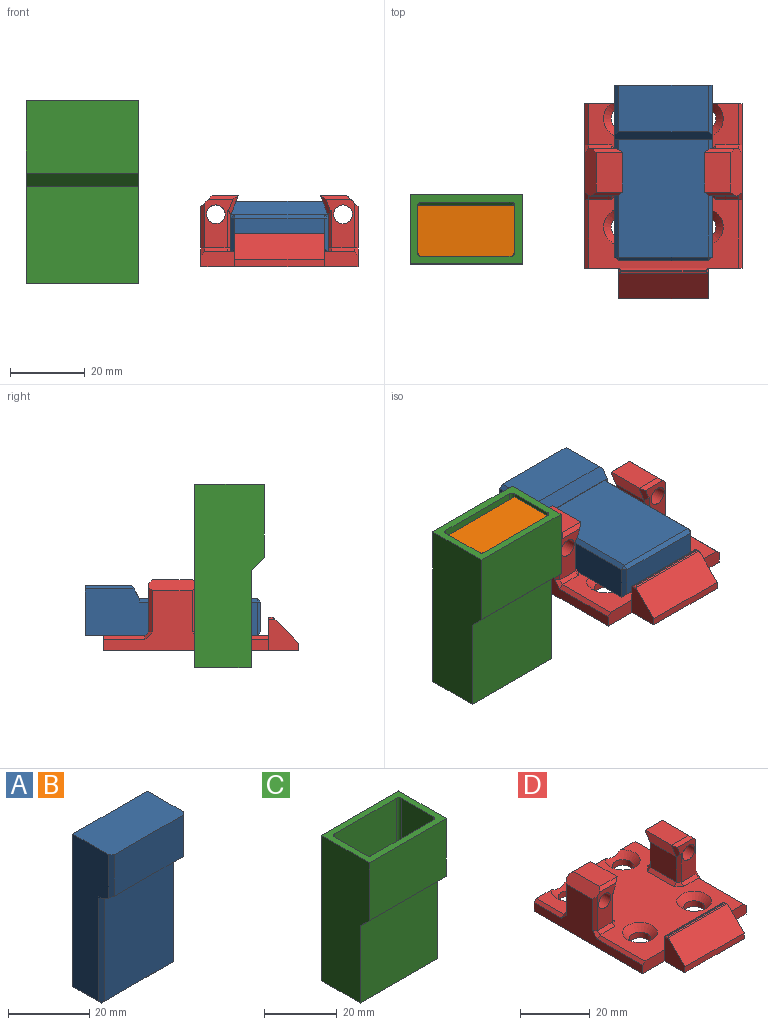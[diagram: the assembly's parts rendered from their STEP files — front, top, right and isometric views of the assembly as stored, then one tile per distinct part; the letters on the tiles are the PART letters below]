
ASSEMBLY  parts=4 mates=2
PART A: 19 faces, bbox 26x13.5x47 mm
  f0: plane 26x13.5mm, normal (0,0,1), area 350mm2, adj f1,f3,f5,f7,f17,f18
  f1: plane 46x12.5mm, normal (-1,0,0), area 463mm2, adj f0,f5,f6,f8,f9,f14,f17
  f2: plane 24x8mm, normal (0,0,-1), area 192mm2, adj f10,f14,f15,f16
  f3: plane 46x12.5mm, normal (1,0,0), area 463mm2, adj f0,f5,f6,f8,f11,f15,f18
  f4: plane 31.5x24mm, normal (0,-1,0), area 756mm2, adj f6,f9,f10,f11
  f5: plane 46x26mm, normal (0,1,0), area 1196mm2, adj f0,f1,f3,f16
  f6: plane 26x1.04mm, normal (0,0,-1), area 1.9mm2, adj f1,f3,f4,f8,f9,f11
  f7: plane 24x12.5mm, normal (0,-1,0), area 300mm2, adj f0,f8,f17,f18
  f8: plane 26x3.46mm, normal (0,-0.5,-0.87), area 102.8mm2, adj f1,f3,f6,f7,f17,f18
  f9: plane 31.5x1mm, normal (-0.71,-0.71,0), area 44.5mm2, adj f1,f4,f6,f12
  f10: plane 24x1mm, normal (0,-0.71,-0.71), area 33.9mm2, adj f2,f4,f12,f13
  f11: plane 31.5x1mm, normal (0.71,-0.71,0), area 44.5mm2, adj f3,f4,f6,f13
  f12: plane 1x1mm, normal (-0.58,-0.58,-0.58), area 0.9mm2, adj f9,f10,f14
  f13: plane 1x1mm, normal (0.58,-0.58,-0.58), area 0.9mm2, adj f10,f11,f15
  f14: plane 9x1mm, normal (-0.71,0,-0.71), area 12mm2, adj f1,f2,f12,f16
  f15: plane 9x1mm, normal (0.71,0,-0.71), area 12mm2, adj f2,f3,f13,f16
  f16: plane 26x1mm, normal (0,0.71,-0.71), area 35.4mm2, adj f2,f5,f14,f15
  f17: plane 13.08x1mm, normal (-0.71,-0.71,0), area 18.1mm2, adj f0,f1,f7,f8
  f18: plane 13.08x1mm, normal (0.71,-0.71,0), area 18.1mm2, adj f0,f3,f7,f8
PART B: same geometry as A
PART C: 29 faces, bbox 30x18.5x49 mm
  f0: plane 30x26mm, normal (0,-1,0), area 780mm2, adj f6,f12,f13,f21
  f1: plane 8x1mm, normal (1,0,0), area 8mm2, adj f2,f4,f5,f6
  f2: plane 23x1mm, normal (0,-1,0), area 23mm2, adj f1,f3,f5,f6
  f3: plane 8x1mm, normal (-1,0,0), area 8mm2, adj f2,f4,f5,f6
  f4: plane 23x1mm, normal (0,1,0), area 23mm2, adj f1,f3,f5,f6
  f5: plane 24x9mm, normal (0,0,1), area 32mm2, adj f1,f2,f3,f4,f14,f15,f16,f17
  f6: plane 30x15mm, normal (0,0,-1), area 266mm2, adj f0,f1,f2,f3,f4,f11,f12,f13
  f7: plane 47x24mm, normal (0,-1,0), area 1128mm2, adj f15,f20,f27,f28
  f8: plane 47x12.5mm, normal (1,0,0), area 493.9mm2, adj f17,f20,f22,f23,f26,f27
  f9: plane 26x24mm, normal (0,1,0), area 624mm2, adj f16,f22,f23,f24
  f10: plane 47x12.5mm, normal (-1,0,0), area 493.9mm2, adj f14,f20,f22,f24,f25,f28
  f11: plane 49x30mm, normal (0,1,0), area 1470mm2, adj f6,f12,f13,f20
  f12: plane 49x18.5mm, normal (-1,0,0), area 809.4mm2, adj f0,f6,f11,f18,f20,f21
  f13: plane 49x18.5mm, normal (1,0,0), area 809.4mm2, adj f0,f6,f11,f18,f20,f21
  f14: plane 10.41x1mm, normal (-0.71,0,0.71), area 13.8mm2, adj f5,f10,f15,f16,f24,f28
  f15: plane 25.41x1mm, normal (0,-0.71,0.71), area 35.1mm2, adj f5,f7,f14,f17,f27,f28
  f16: plane 25.41x1mm, normal (0,0.71,0.71), area 35.1mm2, adj f5,f9,f14,f17,f23,f24
  f17: plane 10.41x1mm, normal (0.71,0,0.71), area 13.8mm2, adj f5,f8,f15,f16,f23,f27
  f18: plane 30x19.5mm, normal (0,-1,0), area 585mm2, adj f12,f13,f20,f21
  f19: plane 24x17.5mm, normal (0,1,0), area 420mm2, adj f20,f22,f25,f26
  f20: plane 30x18.5mm, normal (0,0,1), area 178.9mm2, adj f7,f8,f10,f11,f12,f13,f18,f19
  f21: plane 30x3.5mm, normal (0,-0.71,-0.71), area 148.5mm2, adj f0,f12,f13,f18
  f22: plane 26x4.5mm, normal (0,0.71,0.71), area 128.7mm2, adj f8,f9,f10,f19,f23,f24,f25,f26
  f23: cylinder r=1mm len=26.29mm, axis (0,0,1), area 40.4mm2, adj f8,f9,f16,f17,f22
  f24: cylinder r=1mm len=26.29mm, axis (0,0,-1), area 40.4mm2, adj f9,f10,f14,f16,f22
  f25: cylinder r=1mm len=18.5mm, axis (0,0,-1), area 28.1mm2, adj f10,f19,f20,f22
  f26: cylinder r=1mm len=18.5mm, axis (0,0,1), area 28.1mm2, adj f8,f19,f20,f22
  f27: cylinder r=1mm len=47.29mm, axis (0,0,-1), area 74mm2, adj f7,f8,f15,f17,f20
  f28: cylinder r=1mm len=47.29mm, axis (0,0,1), area 74mm2, adj f7,f10,f14,f15,f20
PART D: 79 faces, bbox 42x53.3x19 mm
  f0: plane 44x40mm, normal (0,0,1), area 1227.8mm2, adj f3,f7,f12,f27,f32,f34,f36,f39
  f1: plane 44x16mm, normal (1,0,0), area 274.3mm2, adj f7,f12,f13,f47,f48,f50,f60,f62
  f2: plane 44x16mm, normal (-1,0,0), area 274.3mm2, adj f3,f12,f13,f27,f28,f30,f42,f43
  f3: plane 9x4mm, normal (0,-1,0), area 35.5mm2, adj f0,f2,f4,f13,f27
  f4: plane 8.4x8.22mm, normal (-1,0,0), area 48.6mm2, adj f3,f5,f13,f72,f74,f76
  f5: plane 24x2mm, normal (0,-1,0), area 48mm2, adj f4,f6,f13,f74
  f6: plane 8.4x8.22mm, normal (1,0,0), area 48.6mm2, adj f5,f7,f13,f72,f74,f77
  f7: plane 9x4mm, normal (0,-1,0), area 35.5mm2, adj f0,f1,f6,f13,f48
  f8: cylinder r=3mm len=6mm, axis (0,0,-1), area 37.7mm2, adj f13,f70
  f9: cylinder r=3mm len=6mm, axis (0,0,-1), area 37.7mm2, adj f13,f71
  f10: cylinder r=3mm len=6mm, axis (0,0,-1), area 37.7mm2, adj f13,f69
  f11: cylinder r=3mm len=6mm, axis (0,0,-1), area 37.7mm2, adj f13,f68
  f12: plane 42x4mm, normal (0,1,0), area 159.2mm2, adj f0,f1,f2,f13,f44,f63,f68,f71
  f13: plane 52.22x42mm, normal (0,0,-1), area 1932.2mm2, adj f1,f2,f3,f4,f5,f6,f7,f8
  f14: plane 13x7.55mm, normal (0,1,0), area 60.8mm2, adj f35,f37,f38,f40,f41,f42,f64,f66
  f15: plane 13x7.55mm, normal (0,-1,0), area 60.8mm2, adj f26,f28,f29,f31,f32,f33,f64,f66
  f16: plane 10.64x9mm, normal (1,0,0), area 95.7mm2, adj f22,f33,f36,f37
  f17: plane 10.64x7mm, normal (0,0,1), area 74.5mm2, adj f23,f26,f40,f64
  f18: plane 13x7.55mm, normal (0,1,0), area 60.8mm2, adj f53,f55,f56,f58,f60,f61,f65,f67
  f19: plane 10.64x9mm, normal (-1,0,0), area 95.7mm2, adj f24,f51,f56,f57
  f20: plane 13x7.55mm, normal (0,-1,0), area 60.8mm2, adj f45,f46,f47,f49,f51,f52,f65,f67
  f21: plane 10.64x7mm, normal (0,0,1), area 74.5mm2, adj f25,f45,f58,f65
  f22: plane 10.64x0.08mm, normal (0,0,-1), area 0.9mm2, adj f16,f23,f31,f35
  f23: plane 10.64x5mm, normal (0.93,0,-0.36), area 57mm2, adj f17,f22,f29,f38
  f24: plane 10.64x0.08mm, normal (0,0,-1), area 0.9mm2, adj f19,f25,f49,f53
  f25: plane 10.64x5mm, normal (-0.93,0,-0.36), area 57mm2, adj f21,f24,f46,f55
  f26: plane 8x1mm, normal (0,-0.71,0.71), area 9.6mm2, adj f15,f17,f29,f64
  f27: plane 18.29x1mm, normal (-0.71,0,0.71), area 25.9mm2, adj f0,f2,f3,f30
  f28: plane 12x1mm, normal (-0.71,-0.71,0), area 16.3mm2, adj f2,f15,f30,f64
  f29: plane 5x2.61mm, normal (0.66,-0.71,-0.25), area 6.1mm2, adj f15,f23,f26,f31
  f30: plane 2x2mm, normal (-0.58,-0.58,0.58), area 2.6mm2, adj f2,f27,f28,f32
  f31: plane 1.08x1mm, normal (0,-0.71,-0.71), area 0.3mm2, adj f15,f22,f29,f33
  f32: plane 6x1mm, normal (0,-0.71,0.71), area 8.5mm2, adj f0,f15,f30,f34
  f33: plane 10x1mm, normal (0.71,-0.71,0), area 13.4mm2, adj f15,f16,f31,f34
  f34: plane 2x2mm, normal (0.58,-0.58,0.58), area 2.6mm2, adj f0,f32,f33,f36
  f35: plane 1.08x1mm, normal (0,0.71,-0.71), area 0.3mm2, adj f14,f22,f37,f38
  f36: plane 10.64x1mm, normal (0.71,0,0.71), area 15mm2, adj f0,f16,f34,f39
  f37: plane 10x1mm, normal (0.71,0.71,0), area 13.4mm2, adj f14,f16,f35,f39
  f38: plane 5x2.61mm, normal (0.66,0.71,-0.25), area 6.1mm2, adj f14,f23,f35,f40
  f39: plane 2x2mm, normal (0.58,0.58,0.58), area 2.6mm2, adj f0,f36,f37,f41
  f40: plane 8x1mm, normal (0,0.71,0.71), area 9.6mm2, adj f14,f17,f38,f64
  f41: plane 6x1mm, normal (0,0.71,0.71), area 8.5mm2, adj f0,f14,f39,f43
  f42: plane 12x1mm, normal (-0.71,0.71,0), area 16.3mm2, adj f2,f14,f43,f64
  f43: plane 2x2mm, normal (-0.58,0.58,0.58), area 2.6mm2, adj f2,f41,f42,f44
  f44: plane 11.07x1mm, normal (-0.71,0,0.71), area 15.7mm2, adj f0,f2,f12,f43
  f45: plane 8x1mm, normal (0,-0.71,0.71), area 9.6mm2, adj f20,f21,f46,f65
  f46: plane 5x2.61mm, normal (-0.66,-0.71,-0.25), area 6.1mm2, adj f20,f25,f45,f49
  f47: plane 12x1mm, normal (0.71,-0.71,0), area 16.3mm2, adj f1,f20,f50,f65
  f48: plane 18.29x1mm, normal (0.71,0,0.71), area 25.9mm2, adj f0,f1,f7,f50
  f49: plane 1.08x1mm, normal (0,-0.71,-0.71), area 0.3mm2, adj f20,f24,f46,f51
  f50: plane 2x2mm, normal (0.58,-0.58,0.58), area 2.6mm2, adj f1,f47,f48,f52
  f51: plane 10x1mm, normal (-0.71,-0.71,0), area 13.4mm2, adj f19,f20,f49,f54
  f52: plane 6x1mm, normal (0,-0.71,0.71), area 8.5mm2, adj f0,f20,f50,f54
  f53: plane 1.08x1mm, normal (0,0.71,-0.71), area 0.3mm2, adj f18,f24,f55,f56
  f54: plane 2x2mm, normal (-0.58,-0.58,0.58), area 2.6mm2, adj f0,f51,f52,f57
  f55: plane 5x2.61mm, normal (-0.66,0.71,-0.25), area 6.1mm2, adj f18,f25,f53,f58
  f56: plane 10x1mm, normal (-0.71,0.71,0), area 13.4mm2, adj f18,f19,f53,f59
  f57: plane 10.64x1mm, normal (-0.71,0,0.71), area 15mm2, adj f0,f19,f54,f59
  f58: plane 8x1mm, normal (0,0.71,0.71), area 9.6mm2, adj f18,f21,f55,f65
  f59: plane 2x2mm, normal (-0.58,0.58,0.58), area 2.6mm2, adj f0,f56,f57,f61
  f60: plane 12x1mm, normal (0.71,0.71,0), area 16.3mm2, adj f1,f18,f62,f65
  f61: plane 6x1mm, normal (0,0.71,0.71), area 8.5mm2, adj f0,f18,f59,f62
  f62: plane 2x2mm, normal (0.58,0.58,0.58), area 2.6mm2, adj f1,f60,f61,f63
  f63: plane 11.07x1mm, normal (0.71,0,0.71), area 15.7mm2, adj f0,f1,f12,f62
  f64: plane 12.64x3mm, normal (-0.71,0,0.71), area 50.8mm2, adj f2,f14,f15,f17,f26,f28,f40,f42
  f65: plane 12.64x3mm, normal (0.71,0,0.71), area 50.8mm2, adj f1,f18,f20,f21,f45,f47,f58,f60
  f66: cylinder r=2.5mm len=12.64mm, axis (0,-1,0), area 198.5mm2, adj f14,f15
  f67: cylinder r=2.5mm len=12.64mm, axis (0,-1,0), area 198.5mm2, adj f18,f20
  f68: cone r=3mm half-angle=45deg, axis (0,0,1), area 65.3mm2, adj f0,f11,f12
  f69: cone r=3mm half-angle=45deg, axis (0,0,1), area 71.1mm2, adj f0,f10
  f70: cone r=3mm half-angle=45deg, axis (0,0,1), area 71.1mm2, adj f0,f8
  f71: cone r=3mm half-angle=45deg, axis (0,0,1), area 65.3mm2, adj f0,f9,f12
  f72: plane 24x4.4mm, normal (0,1,0), area 105.6mm2, adj f0,f4,f6,f75
  f73: plane 22.8x0.37mm, normal (0,0,1), area 8.5mm2, adj f75,f76,f77,f78
  f74: plane 24.04x6.86mm, normal (0,-0.71,0.71), area 231.6mm2, adj f4,f5,f6,f76,f77,f78
  f75: cylinder r=0.6mm len=24mm, axis (1,0,0), area 22.2mm2, adj f72,f73,f76,f77
  f76: cylinder r=0.6mm len=1.82mm, axis (0,1,0), area 1.1mm2, adj f4,f73,f74,f75,f78
  f77: cylinder r=0.6mm len=1.82mm, axis (0,-1,0), area 1.1mm2, adj f6,f73,f74,f75,f78
  f78: cylinder r=0.6mm len=23.65mm, axis (1,0,0), area 10.9mm2, adj f73,f74,f76,f77
PLACE A rot(axis=(-1,0,0),90deg) t=(-64.28,16.63,4)mm
PLACE B rot(axis=(-0.07,0.85,-0.52),0deg) t=(-117.02,-8.92,36.66)mm
PLACE C t=(-0.29,-5.93,-4.54)mm
PLACE D at identity fixed
MATE fastened B.f4 <-> C.f9  axis (0,-1,0) through (-52.74,-18.92,-2.54)mm
MATE planar A.f5 <-> D.f0  axis (0,0,-1) through (0,0.43,4)mm
